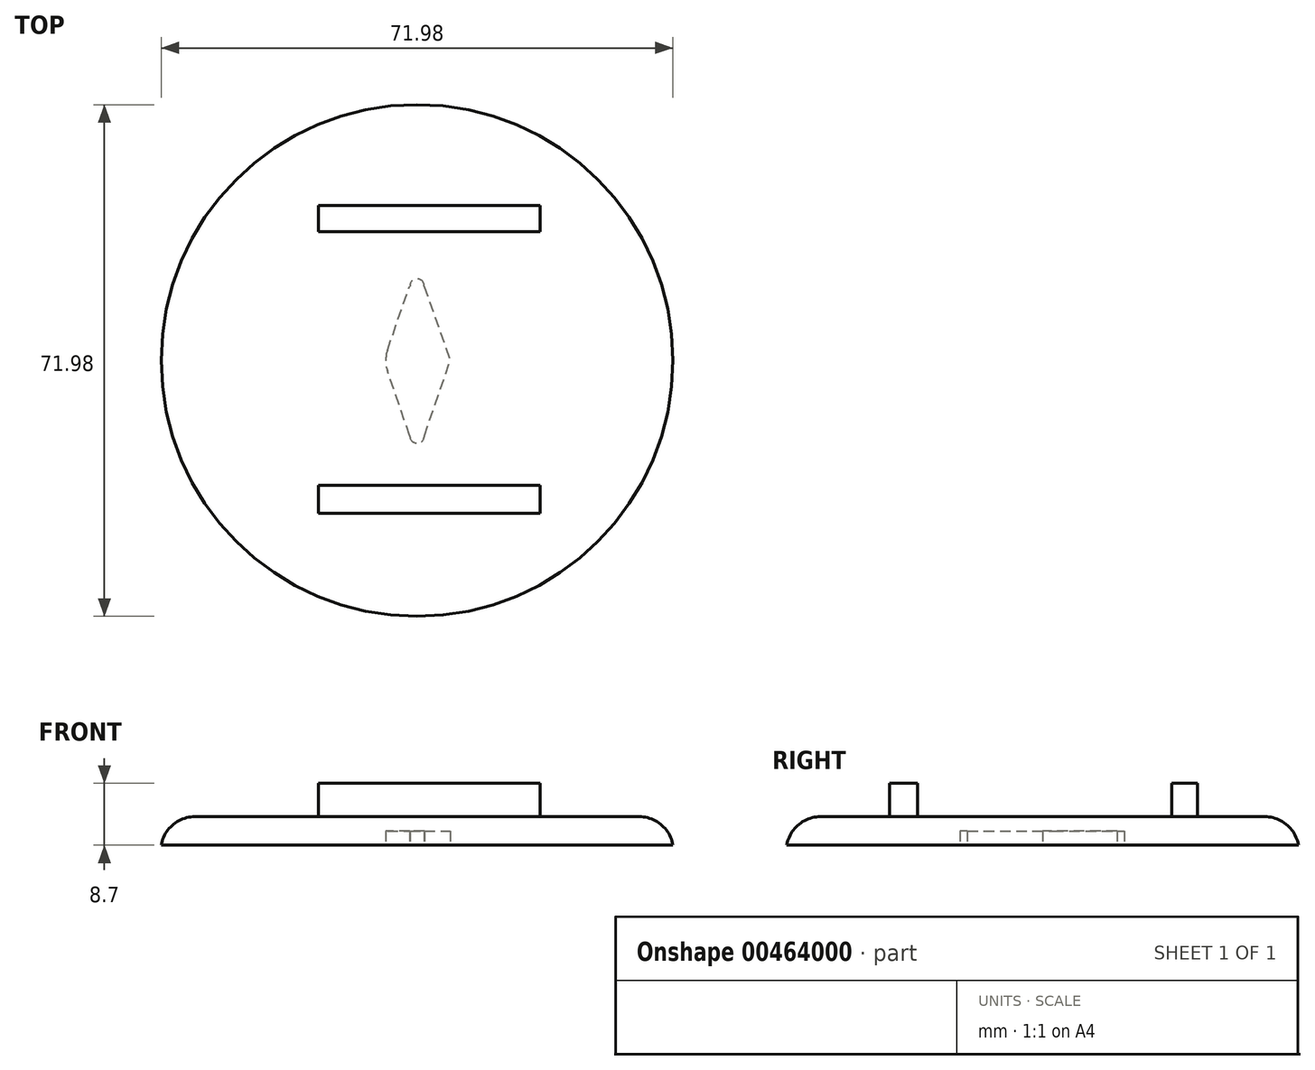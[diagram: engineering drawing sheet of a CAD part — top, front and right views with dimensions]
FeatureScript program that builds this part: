
annotation { "Feature Type Name" : "Feature", "Feature Type Description" : "" }
export const myFeature = defineFeature(function(context is Context, id is Id, definition is map)
    precondition{}
    {
        {
            var Q0;
            Q0=qCreatedBy(makeId("Top.planeOp"),FACE);
            var sketch = newSketch(context, id + "F0", { "sketchPlane" : qUnion([Q0])});
            skCircle(sketch, "E0", {"center": v(0, 0) * mm, "radius": 36 * mm});
            skSolve(sketch);
        }
        {
            var Q0;
            Q0=makeQuery(id+"F0.imprint","IMPRINT",FACE,{"disambiguationData":[TD([[makeQuery(id+"F0.imprint","IMPRINT",EDGE,{"derivedFrom":sQuery(id+"F0.wireOp",EDGE,"E0")}),1.0]])]});
            extrude(context, id + "F1", {"entities" : qUnion([Q0]), "depth" : 4 * mm});
        }
        {
            var Q0;
            Q0=makeQuery(id+"F1.opExtrude","CAP_EDGE",EDGE,{"disambiguationData":[OSD([sQuery(id+"F0.wireOp",EDGE,"E0")])],"isStart":false});
            fillet(context, id + "F2", {"entities" : qUnion([Q0]), "radius" : 4.83 * mm, "tangentPropagation" : true, "allowEdgeOverflow" : false});
        }
        {
            var Q0;
            Q0=makeQuery(id+"F1.opExtrude","CAP_FACE",FACE,{"disambiguationData":[OSD([sQuery(id+"F0.wireOp",EDGE,"E0")])],"isStart":false});
            var sketch = newSketch(context, id + "F3", { "sketchPlane" : qUnion([Q0])});
            skLineSegment(sketch, "E1.bottom", {"start": v(-13.88, 21.81) * mm, "end": v(17.28, 21.81) * mm});
            skLineSegment(sketch, "E1.top", {"start": v(-13.88, 18.13) * mm, "end": v(17.28, 18.13) * mm});
            skLineSegment(sketch, "E1.left", {"start": v(-13.88, 21.81) * mm, "end": v(-13.88, 18.13) * mm});
            skLineSegment(sketch, "E1.right", {"start": v(17.28, 21.81) * mm, "end": v(17.28, 18.13) * mm});
            skLineSegment(sketch, "E2.bottom", {"start": v(-13.88, -17.56) * mm, "end": v(17.28, -17.56) * mm});
            skLineSegment(sketch, "E2.top", {"start": v(-13.88, -21.53) * mm, "end": v(17.28, -21.53) * mm});
            skLineSegment(sketch, "E2.left", {"start": v(-13.88, -17.56) * mm, "end": v(-13.88, -21.53) * mm});
            skLineSegment(sketch, "E2.right", {"start": v(17.28, -17.56) * mm, "end": v(17.28, -21.53) * mm});
            skSolve(sketch);
        }
        {
            var Q0;
            Q0 = qSketchRegion(id + "F3", true);
            extrude(context, id + "F4", {"entities" : qUnion([Q0]), "operationType" : NewBodyOperationType.ADD, "depth" : 4.7 * mm});
        }
        {
            var Q0;
            Q0=makeQuery(id+"F1.opExtrude","CAP_FACE",FACE,{"disambiguationData":[OSD([sQuery(id+"F0.wireOp",EDGE,"E0")])],"isStart":true});
            var sketch = newSketch(context, id + "F5", { "sketchPlane" : qUnion([Q0])});
            skCircle(sketch, "E3", {"center": v(0, 0) * mm, "radius": 4.4 * mm});
            skCircle(sketch, "E4", {"center": v(0, 10.6) * mm, "radius": 1.03 * mm});
            skCircle(sketch, "E5", {"center": v(0, -10.46) * mm, "radius": 1.01 * mm});
            skLineSegment(sketch, "E6", {"start": v(0, -10.46) * mm, "end": v(1.01, -10.46) * mm});
            skLineSegment(sketch, "E7", {"start": v(1.01, -10.46) * mm, "end": v(4.67, 0) * mm});
            skLineSegment(sketch, "E8", {"start": v(0, 10.6) * mm, "end": v(1.03, 10.6) * mm});
            skLineSegment(sketch, "E9", {"start": v(1.03, 10.6) * mm, "end": v(4.67, 0) * mm});
            skLineSegment(sketch, "E10", {"start": v(0, 10.6) * mm, "end": v(-1.03, 10.6) * mm});
            skLineSegment(sketch, "E11", {"start": v(-1.03, 10.6) * mm, "end": v(-4.66, 0) * mm});
            skLineSegment(sketch, "E12", {"start": v(-4.66, 0) * mm, "end": v(-1.08, -10.46) * mm});
            skLineSegment(sketch, "E13", {"start": v(-1.08, -10.46) * mm, "end": v(0, -10.46) * mm});
            skSolve(sketch);
        }
        {
            var Q0;
            {var subQ3=sQuery(id+"F5.wireOp",EDGE,"E3");var subQ7=sQuery(id+"F5.wireOp",EDGE,"E12");var subQ9=makeQuery(id+"F5.imprint","INTERSECT",VERTEX,{"derivedFrom":[subQ3,subQ7]});Q0=makeQuery(id+"F5.imprint","IMPRINT",FACE,{"disambiguationData":[TD([[makeQuery(id+"F5.imprint","IMPRINT",EDGE,{"disambiguationData":[TD([[subQ9,-1.0]])],"derivedFrom":subQ3}),-1.0]])]});}
            var Q1;
            {var subQ0=sQuery(id+"F5.wireOp",EDGE,"E6");Q1=makeQuery(id+"F5.imprint","IMPRINT",FACE,{"disambiguationData":[TD([[makeQuery(id+"F5.imprint","IMPRINT",EDGE,{"derivedFrom":subQ0}),-1.0]])]});}
            var Q2;
            {var subQ0=sQuery(id+"F5.wireOp",EDGE,"E6");Q2=makeQuery(id+"F5.imprint","IMPRINT",FACE,{"disambiguationData":[TD([[makeQuery(id+"F5.imprint","IMPRINT",EDGE,{"derivedFrom":subQ0}),1.0]])]});}
            var Q3;
            {var subQ0=sQuery(id+"F5.wireOp",EDGE,"E3");var subQ1=makeQuery(id+"F5.imprint","INTERSECT",VERTEX,{"derivedFrom":[subQ0,sQuery(id+"F5.wireOp",EDGE,"E12")]});Q3=makeQuery(id+"F5.imprint","IMPRINT",FACE,{"disambiguationData":[TD([[makeQuery(id+"F5.imprint","IMPRINT",EDGE,{"disambiguationData":[TD([[subQ1,1.0]])],"derivedFrom":subQ0}),1.0]])]});}
            var Q4;
            {var subQ0=sQuery(id+"F5.wireOp",EDGE,"E9");Q4=makeQuery(id+"F5.imprint","IMPRINT",FACE,{"disambiguationData":[TD([[makeQuery(id+"F5.imprint","IMPRINT",EDGE,{"derivedFrom":subQ0}),-1.0]])]});}
            var Q5;
            {var subQ0=sQuery(id+"F5.wireOp",EDGE,"E8");Q5=makeQuery(id+"F5.imprint","IMPRINT",FACE,{"disambiguationData":[TD([[makeQuery(id+"F5.imprint","IMPRINT",EDGE,{"derivedFrom":subQ0}),1.0]])]});}
            var Q6;
            {var subQ0=sQuery(id+"F5.wireOp",EDGE,"E8");Q6=makeQuery(id+"F5.imprint","IMPRINT",FACE,{"disambiguationData":[TD([[makeQuery(id+"F5.imprint","IMPRINT",EDGE,{"derivedFrom":subQ0}),-1.0]])]});}
            extrude(context, id + "F6", {"entities" : qUnion([Q0, Q1, Q2, Q3, Q4, Q5, Q6]), "operationType" : NewBodyOperationType.REMOVE, "oppositeDirection" : true, "depth" : 2 * mm});
        }
    });
